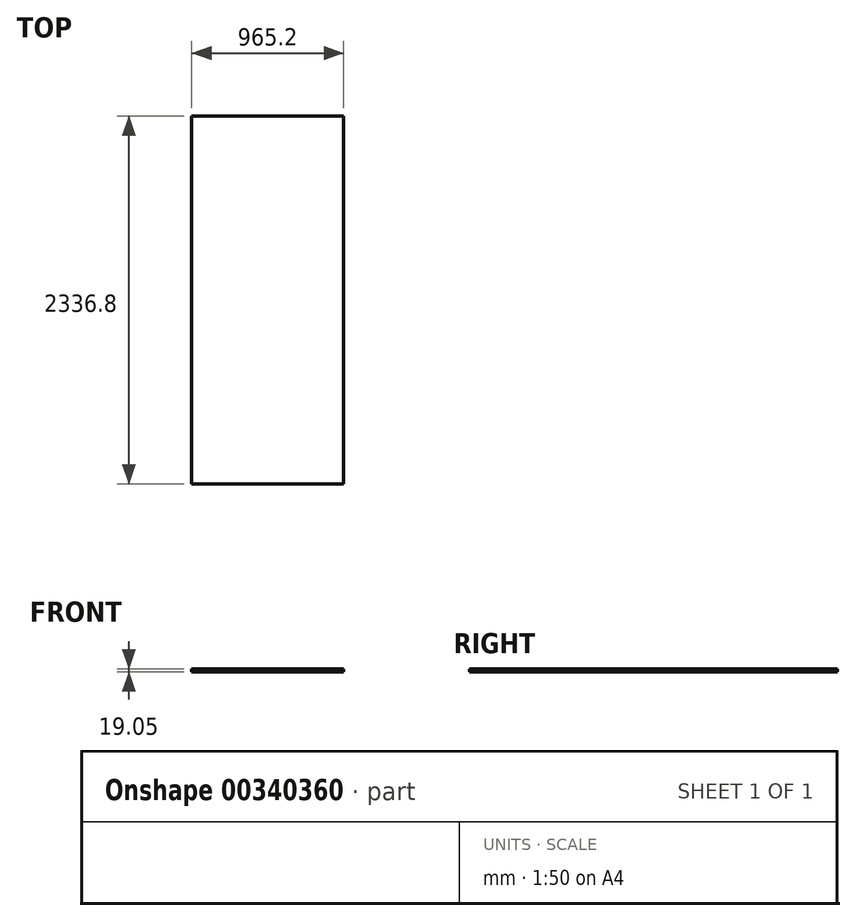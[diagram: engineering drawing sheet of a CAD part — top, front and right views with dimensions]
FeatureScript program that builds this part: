
annotation { "Feature Type Name" : "Feature", "Feature Type Description" : "" }
export const myFeature = defineFeature(function(context is Context, id is Id, definition is map)
    precondition{}
    {
        {
            var Q0;
            Q0=qCreatedBy(makeId("Top.planeOp"),FACE);
            var sketch = newSketch(context, id + "F0", { "sketchPlane" : qUnion([Q0])});
            skLineSegment(sketch, "E0.bottom", {"start": v(-482.6, 1168.4) * mm, "end": v(482.6, 1168.4) * mm});
            skLineSegment(sketch, "E0.top", {"start": v(-482.6, -1168.4) * mm, "end": v(482.6, -1168.4) * mm});
            skLineSegment(sketch, "E0.left", {"start": v(-482.6, 1168.4) * mm, "end": v(-482.6, -1168.4) * mm});
            skLineSegment(sketch, "E0.right", {"start": v(482.6, 1168.4) * mm, "end": v(482.6, -1168.4) * mm});
            skPoint(sketch, "E0.middle", {"position": v(0, 0) * mm});
            skSolve(sketch);
        }
        {
            var Q0;
            Q0=makeQuery(id+"F0.imprint","IMPRINT",FACE,{"disambiguationData":[TD([[makeQuery(id+"F0.imprint","IMPRINT",EDGE,{"derivedFrom":sQuery(id+"F0.wireOp",EDGE,"E0.bottom")}),-1.0]])]});
            extrude(context, id + "F1", {"entities" : qUnion([Q0]), "depth" : 19.05 * mm});
        }
    });
